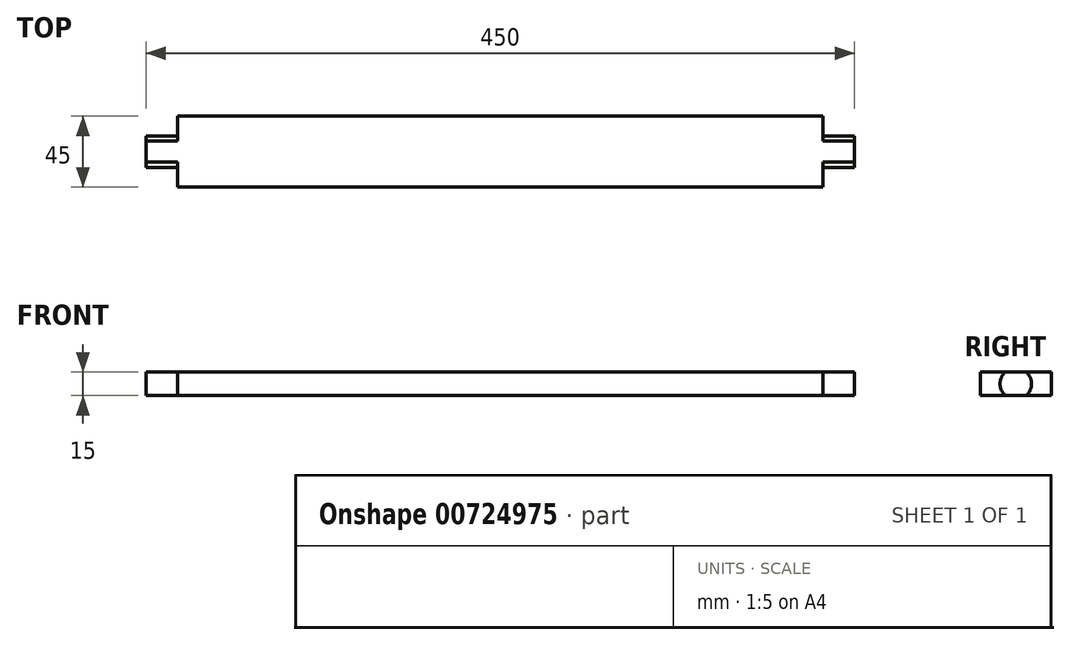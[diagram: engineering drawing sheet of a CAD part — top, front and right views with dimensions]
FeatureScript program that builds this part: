
annotation { "Feature Type Name" : "Feature", "Feature Type Description" : "" }
export const myFeature = defineFeature(function(context is Context, id is Id, definition is map)
    precondition{}
    {
        {
            var Q0;
            Q0=qCreatedBy(makeId("Top.planeOp"),FACE);
            var sketch = newSketch(context, id + "F0", { "sketchPlane" : qUnion([Q0])});
            skLineSegment(sketch, "E0.bottom", {"start": v(-225, 22.5) * mm, "end": v(225, 22.5) * mm});
            skLineSegment(sketch, "E0.top", {"start": v(-225, -22.5) * mm, "end": v(225, -22.5) * mm});
            skLineSegment(sketch, "E0.left", {"start": v(-225, 22.5) * mm, "end": v(-225, -22.5) * mm});
            skLineSegment(sketch, "E0.right", {"start": v(225, 22.5) * mm, "end": v(225, -22.5) * mm});
            skPoint(sketch, "E0.middle", {"position": v(0, 0) * mm});
            skSolve(sketch);
        }
        {
            var Q0;
            Q0=makeQuery(id+"F0.imprint","IMPRINT",FACE,{"disambiguationData":[TD([[makeQuery(id+"F0.imprint","IMPRINT",EDGE,{"derivedFrom":sQuery(id+"F0.wireOp",EDGE,"E0.bottom")}),-1.0]])]});
            extrude(context, id + "F1", {"entities" : qUnion([Q0]), "depth" : 15 * mm, "offsetDistance" : 25 * mm, "symmetric" : true});
        }
        {
            var Q0;
            Q0=makeQuery(id+"F1.opExtrude","SWEPT_FACE",FACE,{"disambiguationData":[OSD([sQuery(id+"F0.wireOp",EDGE,"E0.right")])]});
            var sketch = newSketch(context, id + "F2", { "sketchPlane" : qUnion([Q0])});
            skArc(sketch, "E1", {"start": v(-6.61, 7.5) * mm, "mid": v(-10, 0) * mm, "end": v(-6.61, -7.5) * mm});
            skLineSegment(sketch, "E2.0", {"start": v(22.5, 7.5) * mm, "end": v(22.5, -7.5) * mm});
            skLineSegment(sketch, "E3.0", {"start": v(-22.5, 7.5) * mm, "end": v(-22.5, -7.5) * mm});
            skLineSegment(sketch, "E4", {"start": v(-22.5, 7.5) * mm, "end": v(-6.61, 7.5) * mm});
            skLineSegment(sketch, "E5", {"start": v(-22.5, -7.5) * mm, "end": v(-6.61, -7.5) * mm});
            skArc(sketch, "E6.trimOffspring", {"start": v(6.61, -7.5) * mm, "mid": v(10, 0) * mm, "end": v(6.61, 7.5) * mm});
            skLineSegment(sketch, "E7.trimOffspring", {"start": v(6.61, -7.5) * mm, "end": v(22.5, -7.5) * mm});
            skLineSegment(sketch, "E8.trimOffspring", {"start": v(6.61, 7.5) * mm, "end": v(22.5, 7.5) * mm});
            skSolve(sketch);
        }
        {
            var Q0;
            Q0=makeQuery(id+"F2.imprint","IMPRINT",FACE,{"disambiguationData":[TD([[makeQuery(id+"F2.imprint","IMPRINT",EDGE,{"derivedFrom":sQuery(id+"F2.wireOp",EDGE,"E2.0")}),-1.0]])]});
            var Q1;
            Q1=makeQuery(id+"F2.imprint","IMPRINT",FACE,{"disambiguationData":[TD([[makeQuery(id+"F2.imprint","IMPRINT",EDGE,{"derivedFrom":sQuery(id+"F2.wireOp",EDGE,"E1")}),-1.0]])]});
            extrude(context, id + "F3", {"entities" : qUnion([Q0, Q1]), "operationType" : NewBodyOperationType.REMOVE, "oppositeDirection" : true, "depth" : 20 * mm, "offsetDistance" : 25 * mm});
        }
        {
            var Q0;
            Q0=makeQuery(id+"F1.opExtrude","SWEPT_FACE",FACE,{"disambiguationData":[OSD([sQuery(id+"F0.wireOp",EDGE,"E0.left")])]});
            var sketch = newSketch(context, id + "F4", { "sketchPlane" : qUnion([Q0])});
            skLineSegment(sketch, "E9.0", {"start": v(6.61, 7.5) * mm, "end": v(22.5, 7.5) * mm});
            skArc(sketch, "E10.0.0", {"start": v(6.61, -7.5) * mm, "mid": v(10, 0) * mm, "end": v(6.61, 7.5) * mm});
            skLineSegment(sketch, "E10.0.2", {"start": v(22.5, 7.5) * mm, "end": v(22.5, -7.5) * mm});
            skLineSegment(sketch, "E10.0.3", {"start": v(22.5, -7.5) * mm, "end": v(6.61, -7.5) * mm});
            skArc(sketch, "E11.0.0", {"start": v(-6.61, 7.5) * mm, "mid": v(-10, 0) * mm, "end": v(-6.61, -7.5) * mm});
            skLineSegment(sketch, "E11.0.1", {"start": v(-6.61, -7.5) * mm, "end": v(-22.5, -7.5) * mm});
            skLineSegment(sketch, "E11.0.2", {"start": v(-22.5, -7.5) * mm, "end": v(-22.5, 7.5) * mm});
            skLineSegment(sketch, "E11.0.3", {"start": v(-22.5, 7.5) * mm, "end": v(-6.61, 7.5) * mm});
            skSolve(sketch);
        }
        {
            var Q0;
            Q0=qSketchRegion(id+"F4",true);
            extrude(context, id + "F5", {"entities" : qUnion([Q0]), "operationType" : NewBodyOperationType.REMOVE, "oppositeDirection" : true, "depth" : 20 * mm, "offsetDistance" : 25 * mm});
        }
    });
